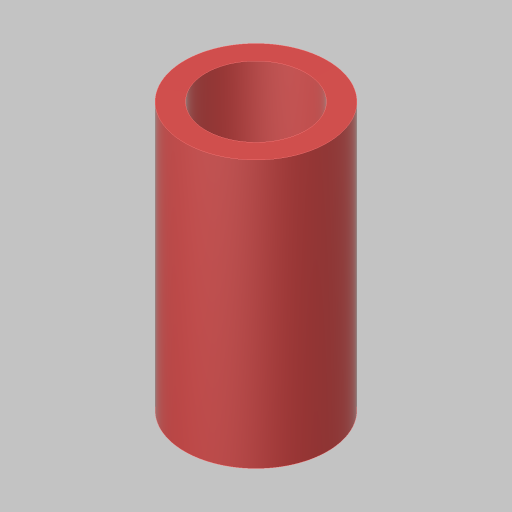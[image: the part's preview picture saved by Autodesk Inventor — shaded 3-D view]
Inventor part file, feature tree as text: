
AUTODESK INVENTOR PART (.ipt)
format: ipt  version: 2023.5 (Build 275446000, 446)  size: 102,912 bytes
history: native  units: in
note: dims shown in document units (in); Inventor stores cm internally (conversion verified against a paired STEP export)
features: extrude x1, sketch x1
ambient origin geometry x8: Origin, YZ Plane, XZ Plane, XY Plane, X Axis, Y Axis, Z Axis, Center Point
bodies: Solid1 (feature_tree)
feature tree (2):
  extrude  "Extrusion1"  Depth=1.555in
  sketch  "Sketch1"  dims[d0=0.58in d1=0.125in d2=1.555in d3=0.0in]
